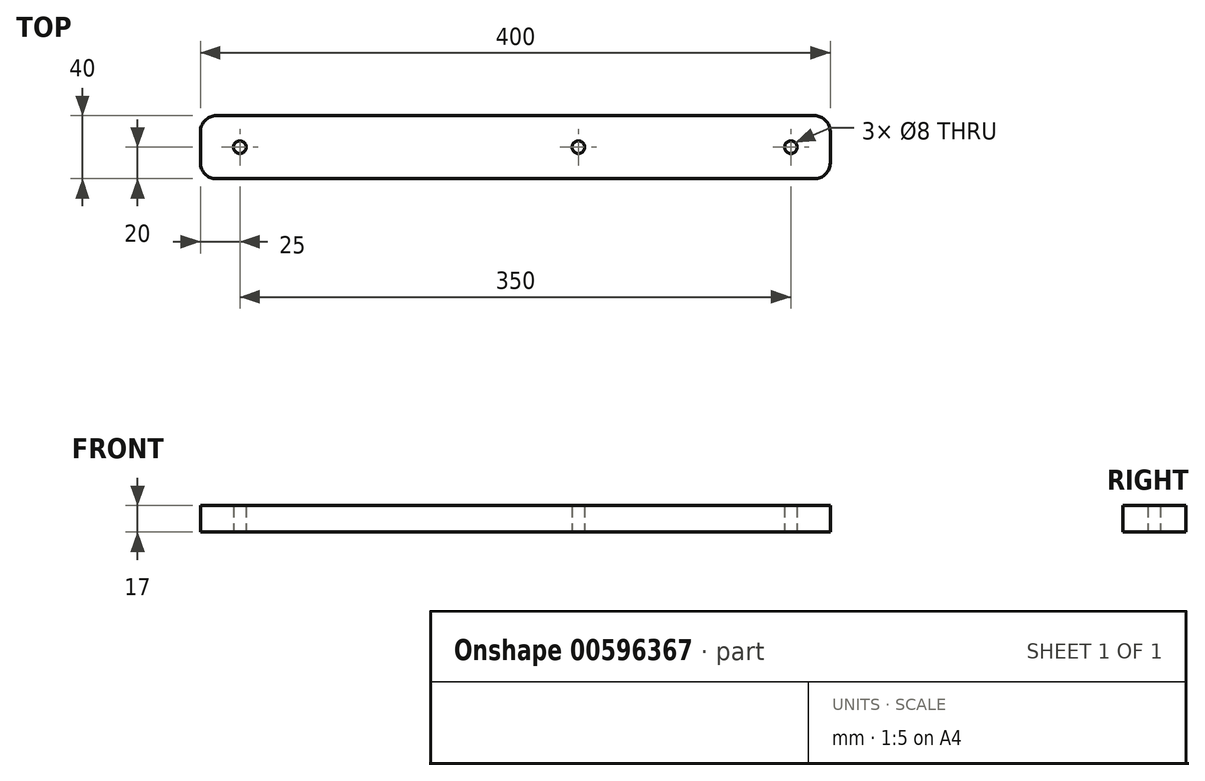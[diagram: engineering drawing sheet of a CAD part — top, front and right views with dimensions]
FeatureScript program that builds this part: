
annotation { "Feature Type Name" : "Feature", "Feature Type Description" : "" }
export const myFeature = defineFeature(function(context is Context, id is Id, definition is map)
    precondition{}
    {
        {
            var Q0;
            Q0=qCreatedBy(makeId("Top.planeOp"),FACE);
            var sketch = newSketch(context, id + "F0", { "sketchPlane" : qUnion([Q0])});
            skLineSegment(sketch, "E0.bottom", {"start": v(190, -20) * mm, "end": v(-190, -20) * mm});
            skLineSegment(sketch, "E0.top", {"start": v(190, 20) * mm, "end": v(-190, 20) * mm});
            skLineSegment(sketch, "E0.left", {"start": v(200, -10) * mm, "end": v(200, 10) * mm});
            skLineSegment(sketch, "E0.right", {"start": v(-200, -10) * mm, "end": v(-200, 10) * mm});
            skPoint(sketch, "E0.middle", {"position": v(0, 0) * mm});
            skCircle(sketch, "E1", {"center": v(40, 0) * mm, "radius": 4 * mm});
            skCircle(sketch, "E2", {"center": v(175, 0) * mm, "radius": 4 * mm});
            skCircle(sketch, "E3", {"center": v(-175, 0) * mm, "radius": 4 * mm});
            skPoint(sketch, "E4.visualSharp", {"position": v(-200, 20) * mm});
            skArc(sketch, "E4.filletArc", {"start": v(-190, 20) * mm, "mid": v(-197.07, 17.07) * mm, "end": v(-200, 10) * mm});
            skPoint(sketch, "E5.visualSharp", {"position": v(-200, -20) * mm});
            skArc(sketch, "E5.filletArc", {"start": v(-200, -10) * mm, "mid": v(-197.07, -17.07) * mm, "end": v(-190, -20) * mm});
            skPoint(sketch, "E6.visualSharp", {"position": v(200, 20) * mm});
            skArc(sketch, "E6.filletArc", {"start": v(200, 10) * mm, "mid": v(197.07, 17.07) * mm, "end": v(190, 20) * mm});
            skPoint(sketch, "E7.visualSharp", {"position": v(200, -20) * mm});
            skArc(sketch, "E7.filletArc", {"start": v(190, -20) * mm, "mid": v(197.07, -17.07) * mm, "end": v(200, -10) * mm});
            skSolve(sketch);
        }
        {
            var Q0;
            Q0=makeQuery(id+"F0.imprint","IMPRINT",FACE,{"disambiguationData":[TD([[makeQuery(id+"F0.imprint","IMPRINT",EDGE,{"derivedFrom":sQuery(id+"F0.wireOp",EDGE,"E0.bottom")}),-1.0]])]});
            extrude(context, id + "F1", {"entities" : qUnion([Q0]), "endBound" : BoundingType.SYMMETRIC, "depth" : 17 * mm, "offsetDistance" : 25 * mm});
        }
    });
